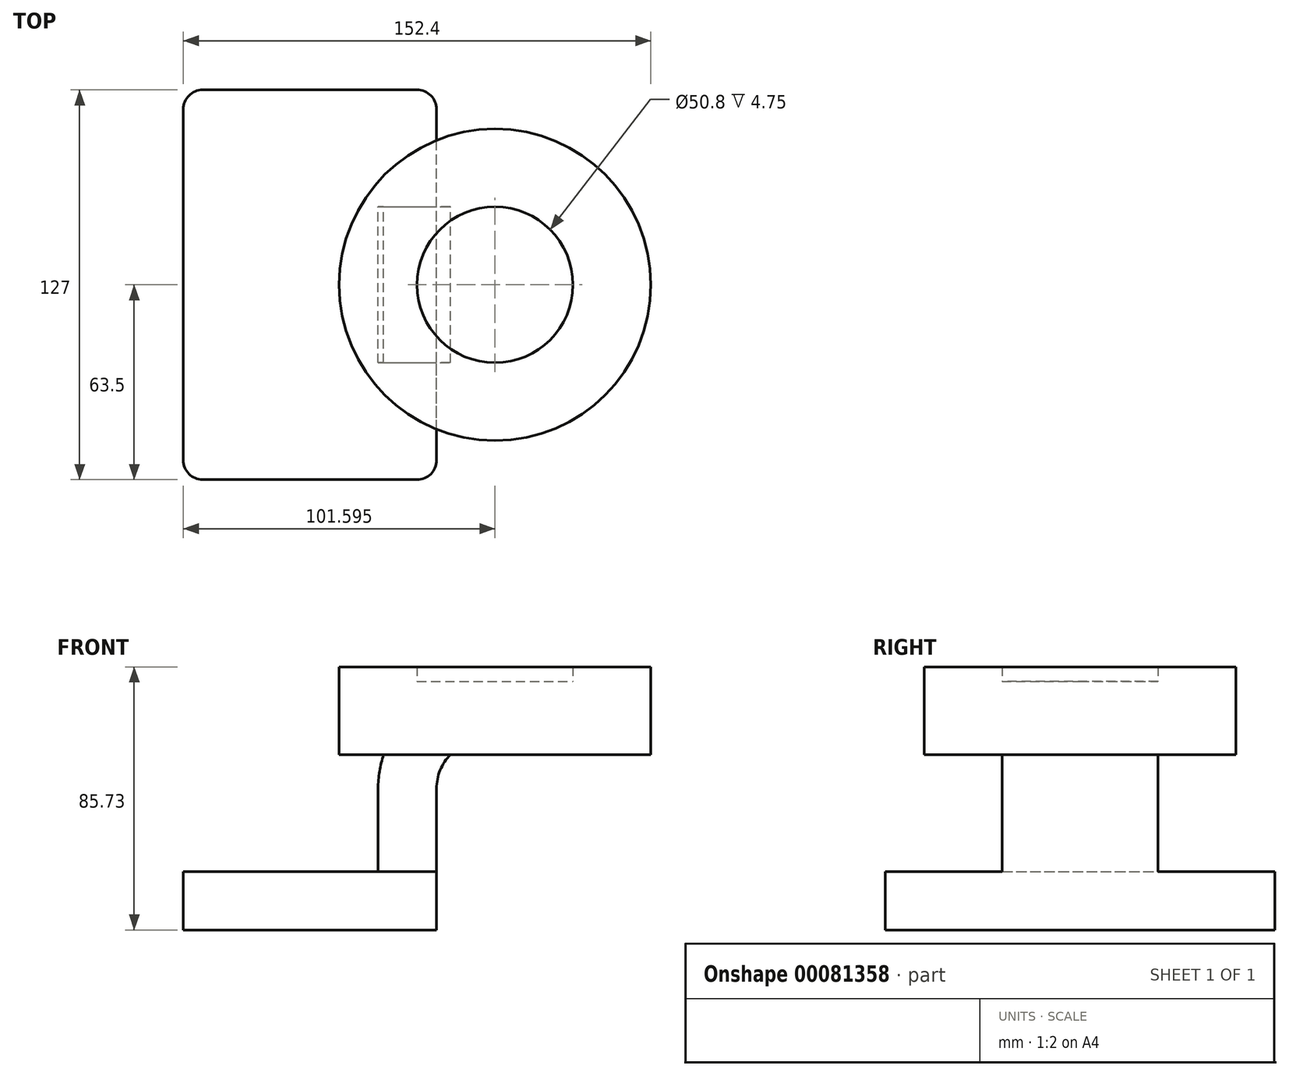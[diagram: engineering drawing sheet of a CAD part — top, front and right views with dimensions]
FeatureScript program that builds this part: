
annotation { "Feature Type Name" : "Feature", "Feature Type Description" : "" }
export const myFeature = defineFeature(function(context is Context, id is Id, definition is map)
    precondition{}
    {
        {
            var Q0;
            Q0=qCreatedBy(makeId("Front.planeOp"),FACE);
            var sketch = newSketch(context, id + "F0", { "sketchPlane" : qUnion([Q0])});
            skLineSegment(sketch, "E0.bottom", {"start": v(-41.28, 9.52) * mm, "end": v(41.27, 9.53) * mm});
            skLineSegment(sketch, "E0.top", {"start": v(-41.28, -9.53) * mm, "end": v(41.28, -9.53) * mm});
            skLineSegment(sketch, "E0.left", {"start": v(-41.28, 9.52) * mm, "end": v(-41.28, -9.53) * mm});
            skLineSegment(sketch, "E0.right", {"start": v(41.27, 9.53) * mm, "end": v(41.28, -9.52) * mm});
            skPoint(sketch, "E0.middle", {"position": v(0, 0) * mm});
            skLineSegment(sketch, "E1", {"start": v(41.27, 9.53) * mm, "end": v(41.27, 36.53) * mm});
            skArc(sketch, "E2", {"start": v(41.27, 36.53) * mm, "mid": v(45.92, 47.75) * mm, "end": v(57.15, 52.4) * mm});
            skLineSegment(sketch, "E3", {"start": v(57.15, 52.4) * mm, "end": v(87.12, 52.4) * mm});
            skLineSegment(sketch, "E4.bottom", {"start": v(60.32, 47.63) * mm, "end": v(111.12, 47.63) * mm});
            skLineSegment(sketch, "E4.top", {"start": v(60.32, 76.2) * mm, "end": v(111.12, 76.2) * mm});
            skLineSegment(sketch, "E4.left", {"start": v(60.32, 47.63) * mm, "end": v(60.32, 76.2) * mm});
            skLineSegment(sketch, "E4.right", {"start": v(111.12, 47.63) * mm, "end": v(111.12, 76.2) * mm});
            skPoint(sketch, "E4.middle", {"position": v(85.72, 61.91) * mm});
            skLineSegment(sketch, "E5.0", {"start": v(57.15, 71.45) * mm, "end": v(87.12, 71.45) * mm});
            skArc(sketch, "E5.1", {"start": v(22.22, 36.53) * mm, "mid": v(32.45, 61.22) * mm, "end": v(57.15, 71.45) * mm});
            skLineSegment(sketch, "E5.2", {"start": v(22.22, 9.53) * mm, "end": v(22.22, 36.53) * mm});
            skLineSegment(sketch, "E6", {"start": v(85.72, 61.91) * mm, "end": v(85.72, 76.2) * mm});
            skFitSpline(sketch, "E7", {"points": [v(-41.28, 9.52) * mm, v(57.15, 71.45) * mm], "startDerivative": vector(27.16, 106.66) * mm, "endDerivative": vector(134.78, -2.12) * mm});
            skSolve(sketch);
        }
        {
            var Q0;
            Q0=makeQuery(id+"F0.imprint","IMPRINT",FACE,{"disambiguationData":[TD([[makeQuery(id+"F0.imprint","IMPRINT",EDGE,{"derivedFrom":sQuery(id+"F0.wireOp",EDGE,"E0.top")}),1.0]])]});
            extrude(context, id + "F1", {"entities" : qUnion([Q0]), "endBound" : BoundingType.SYMMETRIC, "depth" : 127 * mm});
        }
        {
            var Q0;
            {var subQ6=sQuery(id+"F0.wireOp",EDGE,"E1");Q0=makeQuery(id+"F0.imprint","IMPRINT",FACE,{"disambiguationData":[TD([[makeQuery(id+"F0.imprint","IMPRINT",EDGE,{"derivedFrom":subQ6}),1.0]])]});}
            extrude(context, id + "F2", {"entities" : qUnion([Q0]), "operationType" : NewBodyOperationType.ADD, "endBound" : BoundingType.SYMMETRIC, "depth" : 50.8 * mm});
        }
        {
            var Q0;
            Q0=makeQuery(id+"F0.imprint","IMPRINT",FACE,{"disambiguationData":[TD([[makeQuery(id+"F0.imprint","IMPRINT",EDGE,{"derivedFrom":sQuery(id+"F0.wireOp",EDGE,"E5.1")}),1.0]])]});
            extrude(context, id + "F3", {"entities" : qUnion([Q0]), "operationType" : NewBodyOperationType.ADD, "endBound" : BoundingType.SYMMETRIC, "depth" : 15.88 * mm});
        }
        {
            var Q0;
            {var subQ6=sQuery(id+"F0.wireOp",EDGE,"E4.bottom");Q0=makeQuery(id+"F0.imprint","IMPRINT",FACE,{"disambiguationData":[TD([[makeQuery(id+"F0.imprint","IMPRINT",EDGE,{"derivedFrom":subQ6}),1.0]])]});}
            var Q1;
            Q1=sQuery(id+"F0.wireOp",EDGE,"E4.left");
            revolve(context, id + "F4", {"operationType" : NewBodyOperationType.ADD, "entities" : qUnion([Q0]), "axis" : qUnion([Q1]), "revolveType" : RevolveType.FULL});
        }
        {
            var Q0;
            Q0=makeQuery(id+"F1.opExtrude","CAP_EDGE",EDGE,{"disambiguationData":[OSD([sQuery(id+"F0.wireOp",EDGE,"E0.right")])],"isStart":false});
            var Q1;
            Q1=makeQuery(id+"F1.opExtrude","CAP_EDGE",EDGE,{"disambiguationData":[OSD([sQuery(id+"F0.wireOp",EDGE,"E0.left")])],"isStart":false});
            var Q2;
            Q2=makeQuery(id+"F1.opExtrude","CAP_EDGE",EDGE,{"disambiguationData":[OSD([sQuery(id+"F0.wireOp",EDGE,"E0.right")])],"isStart":true});
            var Q3;
            Q3=makeQuery(id+"F1.opExtrude","CAP_EDGE",EDGE,{"disambiguationData":[OSD([sQuery(id+"F0.wireOp",EDGE,"E0.left")])],"isStart":true});
            fillet(context, id + "F5", {"entities" : qUnion([Q0, Q1, Q2, Q3]), "radius" : 6.35 * mm, "tangentPropagation" : true, "allowEdgeOverflow" : false});
        }
    });
